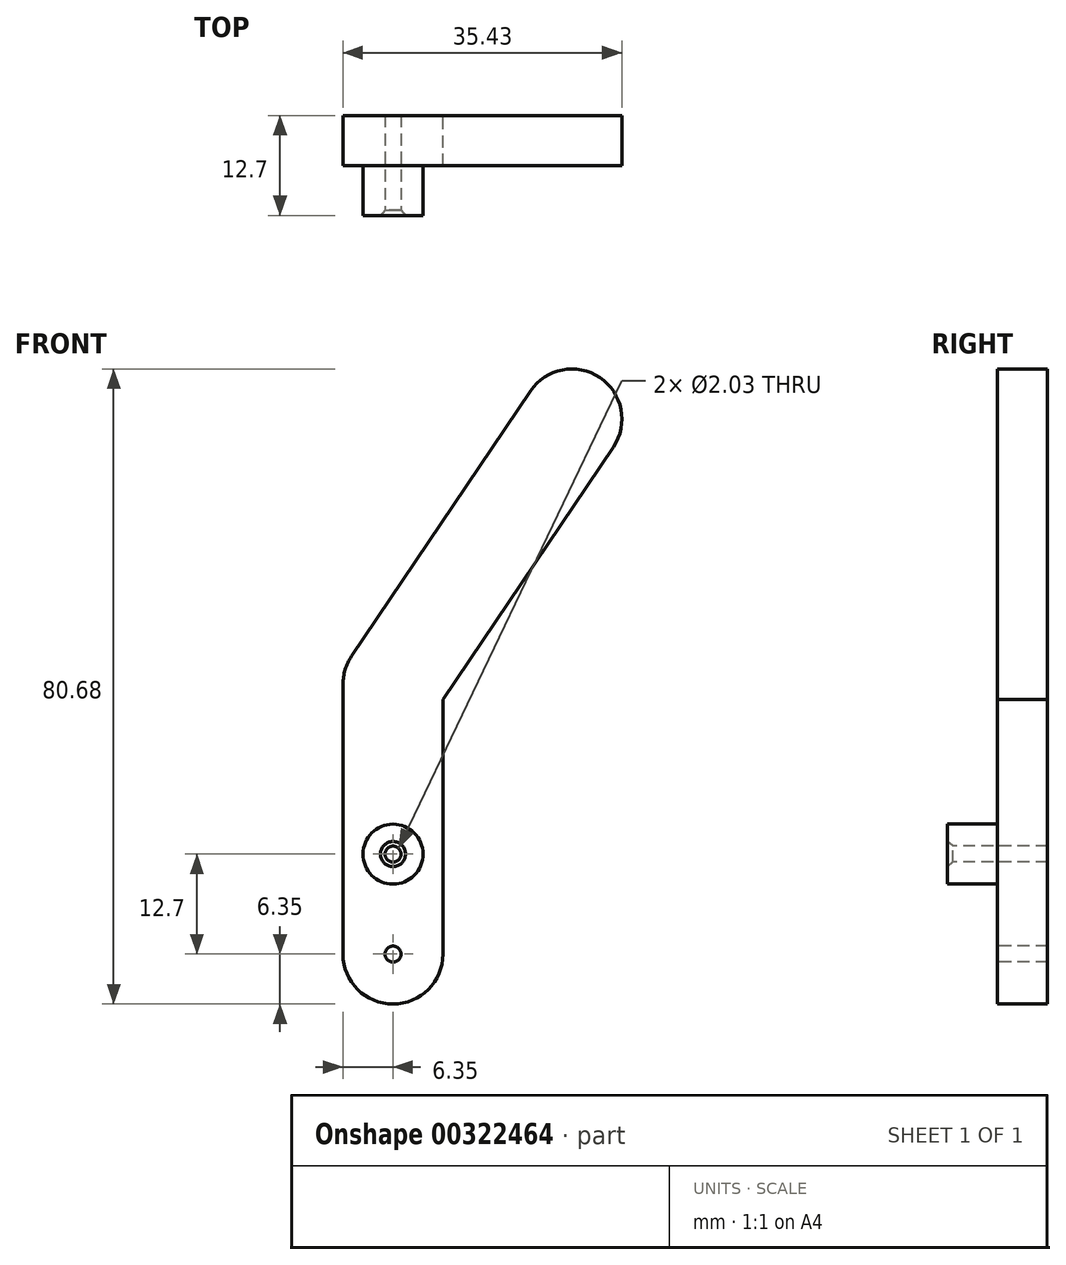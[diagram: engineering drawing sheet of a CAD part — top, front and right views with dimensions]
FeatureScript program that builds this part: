
annotation { "Feature Type Name" : "Feature", "Feature Type Description" : "" }
export const myFeature = defineFeature(function(context is Context, id is Id, definition is map)
    precondition{}
    {
        {
            var Q0;
            Q0=qCreatedBy(makeId("Front.planeOp"),FACE);
            var sketch = newSketch(context, id + "F0", { "sketchPlane" : qUnion([Q0])});
            skLineSegment(sketch, "E0", {"start": v(0, 0) * mm, "end": v(0, -21.59) * mm});
            skLineSegment(sketch, "E1", {"start": v(0, -21.59) * mm, "end": v(0, -34.3) * mm});
            skLineSegment(sketch, "E2", {"start": v(0, 0) * mm, "end": v(22.73, 33.7) * mm});
            skArc(sketch, "E3.0.startCap", {"start": v(5.26, -3.55) * mm, "mid": v(-3.55, -5.26) * mm, "end": v(-5.26, 3.55) * mm});
            skArc(sketch, "E3.0.endCap", {"start": v(17.46, 37.24) * mm, "mid": v(26.28, 38.96) * mm, "end": v(27.99, 30.14) * mm});
            skLineSegment(sketch, "E3.0.left", {"start": v(-5.26, 3.55) * mm, "end": v(17.46, 37.24) * mm});
            skLineSegment(sketch, "E3.0.right", {"start": v(5.26, -3.55) * mm, "end": v(27.99, 30.14) * mm});
            skArc(sketch, "E3.1.startCap", {"start": v(-6.35, 0) * mm, "mid": v(0, 6.35) * mm, "end": v(6.35, 0) * mm});
            skArc(sketch, "E3.1.endCap", {"start": v(6.35, -21.59) * mm, "mid": v(0, -27.94) * mm, "end": v(-6.35, -21.59) * mm});
            skLineSegment(sketch, "E3.1.left", {"start": v(6.35, 0) * mm, "end": v(6.35, -21.59) * mm});
            skLineSegment(sketch, "E3.1.right", {"start": v(-6.35, 0) * mm, "end": v(-6.35, -21.59) * mm});
            skArc(sketch, "E3.2.startCap", {"start": v(-6.35, -21.59) * mm, "mid": v(0, -15.24) * mm, "end": v(6.35, -21.59) * mm});
            skArc(sketch, "E3.2.endCap", {"start": v(6.35, -34.3) * mm, "mid": v(0, -40.64) * mm, "end": v(-6.35, -34.3) * mm});
            skLineSegment(sketch, "E3.2.left", {"start": v(6.35, -21.59) * mm, "end": v(6.35, -34.3) * mm});
            skLineSegment(sketch, "E3.2.right", {"start": v(-6.35, -21.59) * mm, "end": v(-6.35, -34.3) * mm});
            skSolve(sketch);
        }
        {
            var Q0;
            Q0 = qSketchRegion(id + "F0", true);
            extrude(context, id + "F1", {"entities" : qUnion([Q0]), "depth" : 6.35 * mm});
        }
        {
            var Q0;
            Q0=makeQuery(id+"F1.opExtrude","CAP_FACE",FACE,{"disambiguationData":[OSD([sQuery(id+"F0.wireOp",EDGE,"E3.0.endCap"),sQuery(id+"F0.wireOp",EDGE,"E3.0.left"),sQuery(id+"F0.wireOp",EDGE,"E3.0.right"),sQuery(id+"F0.wireOp",EDGE,"E3.1.startCap"),sQuery(id+"F0.wireOp",EDGE,"E3.1.left"),sQuery(id+"F0.wireOp",EDGE,"E3.1.right"),sQuery(id+"F0.wireOp",EDGE,"E3.2.endCap"),sQuery(id+"F0.wireOp",EDGE,"E3.2.left"),sQuery(id+"F0.wireOp",EDGE,"E3.2.right")])],"isStart":false});
            var sketch = newSketch(context, id + "F2", { "sketchPlane" : qUnion([Q0])});
            skCircle(sketch, "E4", {"center": v(0, -21.59) * mm, "radius": 3.81 * mm});
            skSolve(sketch);
        }
        {
            var Q0;
            Q0 = qSketchRegion(id + "F2", true);
            extrude(context, id + "F3", {"entities" : qUnion([Q0]), "operationType" : NewBodyOperationType.ADD, "depth" : 6.35 * mm});
        }
        {
            var Q0;
            Q0=makeQuery(id+"F3.opExtrude","CAP_FACE",FACE,{"disambiguationData":[OSD([sQuery(id+"F2.wireOp",EDGE,"E4")])],"isStart":false});
            var sketch = newSketch(context, id + "F4", { "sketchPlane" : qUnion([Q0])});
            skPoint(sketch, "E5", {"position": v(0, -21.59) * mm});
            skSolve(sketch);
        }
        {
            var Q0;
            Q0=sQuery(id+"F4.wireOp",VERTEX,"E5");
            var Q1;
            Q1=makeQuery(id+"F1.opExtrude","SWEPT_BODY",BODY,{"disambiguationData":[OSD([sQuery(id+"F0.wireOp",EDGE,"E3.0.endCap"),sQuery(id+"F0.wireOp",EDGE,"E3.0.left"),sQuery(id+"F0.wireOp",EDGE,"E3.0.right"),sQuery(id+"F0.wireOp",EDGE,"E3.1.startCap"),sQuery(id+"F0.wireOp",EDGE,"E3.1.left"),sQuery(id+"F0.wireOp",EDGE,"E3.1.right"),sQuery(id+"F0.wireOp",EDGE,"E3.2.endCap"),sQuery(id+"F0.wireOp",EDGE,"E3.2.left"),sQuery(id+"F0.wireOp",EDGE,"E3.2.right")])]});
            hole(context, id + "F5", {"style" : HoleStyle.C_SINK, "endStyle" : HoleEndStyle.THROUGH, "holeDiameter" : 2.03 * mm, "cSinkDiameter" : 3.17 * mm, "cSinkAngle" : 82 * degree, "tappedDepth" : 12.7 * mm, "tapClearance" : 3, "locations" : qUnion([Q0]), "scope" : qUnion([Q1])});
        }
        {
            var Q0;
            Q0=makeQuery(id+"F1.opExtrude","CAP_FACE",FACE,{"disambiguationData":[OSD([sQuery(id+"F0.wireOp",EDGE,"E3.0.endCap"),sQuery(id+"F0.wireOp",EDGE,"E3.0.left"),sQuery(id+"F0.wireOp",EDGE,"E3.0.right"),sQuery(id+"F0.wireOp",EDGE,"E3.1.startCap"),sQuery(id+"F0.wireOp",EDGE,"E3.1.left"),sQuery(id+"F0.wireOp",EDGE,"E3.1.right"),sQuery(id+"F0.wireOp",EDGE,"E3.2.endCap"),sQuery(id+"F0.wireOp",EDGE,"E3.2.left"),sQuery(id+"F0.wireOp",EDGE,"E3.2.right")])],"isStart":false});
            var sketch = newSketch(context, id + "F6", { "sketchPlane" : qUnion([Q0])});
            skPoint(sketch, "E6", {"position": v(0, -34.3) * mm});
            skSolve(sketch);
        }
        {
            var Q0;
            Q0=sQuery(id+"F6.wireOp",VERTEX,"E6");
            var Q1;
            Q1=makeQuery(id+"F1.opExtrude","SWEPT_BODY",BODY,{"disambiguationData":[OSD([sQuery(id+"F0.wireOp",EDGE,"E3.0.endCap"),sQuery(id+"F0.wireOp",EDGE,"E3.0.left"),sQuery(id+"F0.wireOp",EDGE,"E3.0.right"),sQuery(id+"F0.wireOp",EDGE,"E3.1.startCap"),sQuery(id+"F0.wireOp",EDGE,"E3.1.left"),sQuery(id+"F0.wireOp",EDGE,"E3.1.right"),sQuery(id+"F0.wireOp",EDGE,"E3.2.endCap"),sQuery(id+"F0.wireOp",EDGE,"E3.2.left"),sQuery(id+"F0.wireOp",EDGE,"E3.2.right")])]});
            hole(context, id + "F7", {"style" : HoleStyle.SIMPLE, "endStyle" : HoleEndStyle.THROUGH, "holeDiameter" : 2.03 * mm, "tappedDepth" : 12.7 * mm, "tapClearance" : 3, "locations" : qUnion([Q0]), "scope" : qUnion([Q1])});
        }
    });
